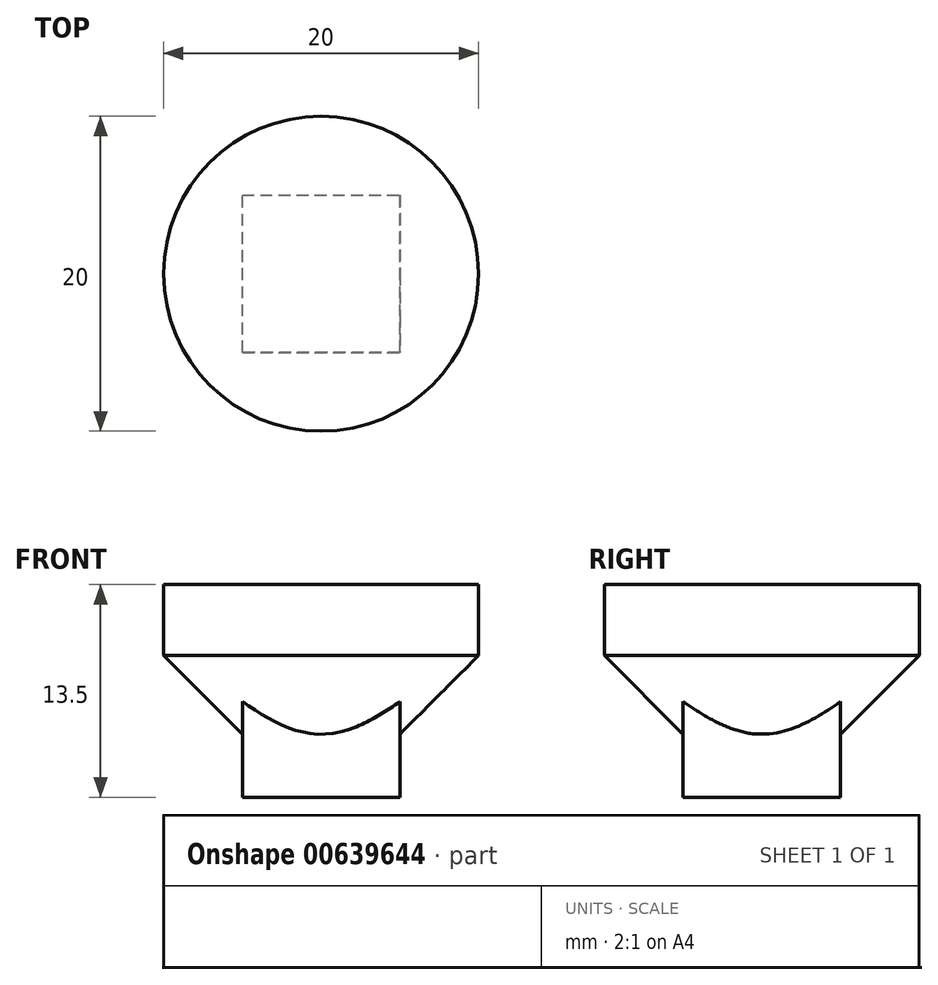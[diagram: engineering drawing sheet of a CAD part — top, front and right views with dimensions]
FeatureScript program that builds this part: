
annotation { "Feature Type Name" : "Feature", "Feature Type Description" : "" }
export const myFeature = defineFeature(function(context is Context, id is Id, definition is map)
    precondition{}
    {
        {
            var Q0;
            Q0=qCreatedBy(makeId("Top.planeOp"),FACE);
            var sketch = newSketch(context, id + "F0", { "sketchPlane" : qUnion([Q0])});
            skPoint(sketch, "E0.middle", {"position": v(0, 0) * mm});
            skLineSegment(sketch, "E1.bottom", {"start": v(5, 5) * mm, "end": v(-5, 5) * mm});
            skLineSegment(sketch, "E1.top", {"start": v(5, -5) * mm, "end": v(-5, -5) * mm});
            skLineSegment(sketch, "E1.left", {"start": v(5, 5) * mm, "end": v(5, -5) * mm});
            skLineSegment(sketch, "E1.right", {"start": v(-5, 5) * mm, "end": v(-5, -5) * mm});
            skLineSegment(sketch, "E2.bottom", {"start": v(-20.5, 20.5) * mm, "end": v(20.5, 20.5) * mm});
            skLineSegment(sketch, "E2.top", {"start": v(-20.5, -20.5) * mm, "end": v(20.5, -20.5) * mm});
            skLineSegment(sketch, "E2.left", {"start": v(-20.5, 20.5) * mm, "end": v(-20.5, -20.5) * mm});
            skLineSegment(sketch, "E2.right", {"start": v(20.5, 20.5) * mm, "end": v(20.5, -20.5) * mm});
            skSolve(sketch);
        }
        {
            var Q0;
            {var subQ1=sQuery(id+"F0.wireOp",EDGE,"E1.right");Q0=makeQuery(id+"F0.imprint","IMPRINT",FACE,{"disambiguationData":[TD([[makeQuery(id+"F0.imprint","IMPRINT",EDGE,{"derivedFrom":subQ1}),-1.0]])]});}
            var Q1;
            {var subQ1=sQuery(id+"F0.wireOp",EDGE,"E1.top");Q1=makeQuery(id+"F0.imprint","IMPRINT",FACE,{"disambiguationData":[TD([[makeQuery(id+"F0.imprint","IMPRINT",EDGE,{"derivedFrom":subQ1}),1.0]])]});}
            var Q2;
            {var subQ1=sQuery(id+"F0.wireOp",EDGE,"E1.left");Q2=makeQuery(id+"F0.imprint","IMPRINT",FACE,{"disambiguationData":[TD([[makeQuery(id+"F0.imprint","IMPRINT",EDGE,{"derivedFrom":subQ1}),1.0]])]});}
            var Q3;
            {var subQ5=sQuery(id+"F0.wireOp",EDGE,"E1.bottom");Q3=makeQuery(id+"F0.imprint","IMPRINT",FACE,{"disambiguationData":[TD([[makeQuery(id+"F0.imprint","IMPRINT",EDGE,{"derivedFrom":subQ5}),-1.0]])]});}
            var Q4;
            Q4=makeQuery(id+"F0.imprint","IMPRINT",FACE,{"disambiguationData":[TD([[makeQuery(id+"F0.imprint","IMPRINT",EDGE,{"derivedFrom":sQuery(id+"F0.wireOp",EDGE,"E1.bottom")}),1.0]])]});
            extrude(context, id + "F1", {"entities" : qUnion([Q0, Q1, Q2, Q3, Q4]), "depth" : 10 * mm, "offsetDistance" : 25 * mm});
        }
        {
            var Q0;
            Q0=makeQuery(id+"F0.imprint","IMPRINT",FACE,{"disambiguationData":[TD([[makeQuery(id+"F0.imprint","IMPRINT",EDGE,{"derivedFrom":sQuery(id+"F0.wireOp",EDGE,"E1.bottom")}),1.0]])]});
            extrude(context, id + "F2", {"entities" : qUnion([Q0]), "operationType" : NewBodyOperationType.ADD, "depth" : 25 * mm, "offsetDistance" : 25 * mm});
        }
        {
            var Q0;
            Q0=makeQuery(id+"F2.opExtrude","CAP_FACE",FACE,{"disambiguationData":[OSD([sQuery(id+"F0.wireOp",EDGE,"E1.bottom"),sQuery(id+"F0.wireOp",EDGE,"E1.top"),sQuery(id+"F0.wireOp",EDGE,"E1.left"),sQuery(id+"F0.wireOp",EDGE,"E1.right")])],"isStart":false});
            var sketch = newSketch(context, id + "F3", { "sketchPlane" : qUnion([Q0])});
            skLineSegment(sketch, "E3", {"start": v(-5, 5) * mm, "end": v(-5, -5) * mm});
            skPoint(sketch, "E4.middle", {"position": v(0, 0) * mm});
            skCircle(sketch, "E5", {"center": v(0, 0) * mm, "radius": 10 * mm});
            skSolve(sketch);
        }
        {
            var Q0;
            Q0=qSketchRegion(id+"F3",true);
            extrude(context, id + "F4", {"entities" : qUnion([Q0]), "operationType" : NewBodyOperationType.ADD, "oppositeDirection" : true, "depth" : 8 * mm, "offsetDistance" : 25 * mm});
        }
        {
            var Q0;
            Q0=makeQuery(id+"F1.opExtrude","CAP_FACE",FACE,{"disambiguationData":[OSD([sQuery(id+"F0.wireOp",EDGE,"E2.bottom"),sQuery(id+"F0.wireOp",EDGE,"E2.top"),sQuery(id+"F0.wireOp",EDGE,"E2.left"),sQuery(id+"F0.wireOp",EDGE,"E2.right")])],"isStart":true});
            var sketch = newSketch(context, id + "F5", { "sketchPlane" : qUnion([Q0])});
            skLineSegment(sketch, "E6.bottom", {"start": v(5, 5) * mm, "end": v(-5, 5) * mm});
            skLineSegment(sketch, "E6.top", {"start": v(5, -5) * mm, "end": v(-5, -5) * mm});
            skLineSegment(sketch, "E6.left", {"start": v(5, 5) * mm, "end": v(5, -5) * mm});
            skLineSegment(sketch, "E6.right", {"start": v(-5, 5) * mm, "end": v(-5, -5) * mm});
            skPoint(sketch, "E6.middle", {"position": v(0, 0) * mm});
            skPoint(sketch, "E7", {"position": v(5, 5) * mm});
            skPoint(sketch, "E8", {"position": v(-5, 5) * mm});
            skPoint(sketch, "E9", {"position": v(-5, -5) * mm});
            skPoint(sketch, "E10", {"position": v(5, -5) * mm});
            skLineSegment(sketch, "E11", {"start": v(0, 16.62) * mm, "end": v(0, 20.5) * mm});
            skLineSegment(sketch, "E12", {"start": v(-16.62, 0) * mm, "end": v(-20.5, 0) * mm});
            skLineSegment(sketch, "E13", {"start": v(0, -16.62) * mm, "end": v(0, -20.5) * mm});
            skLineSegment(sketch, "E14", {"start": v(16.62, 0) * mm, "end": v(20.5, 0) * mm});
            skArc(sketch, "E15", {"start": v(0, -20.5) * mm, "mid": v(13.15, -14.18) * mm, "end": v(16.62, 0) * mm});
            skArc(sketch, "E16", {"start": v(20.5, 0) * mm, "mid": v(14.2, 13.18) * mm, "end": v(0, 16.62) * mm});
            skArc(sketch, "E17", {"start": v(0, 20.5) * mm, "mid": v(-13.16, 14.18) * mm, "end": v(-16.62, 0) * mm});
            skArc(sketch, "E18", {"start": v(-20.5, 0) * mm, "mid": v(-14.2, -13.17) * mm, "end": v(0, -16.62) * mm});
            skSolve(sketch);
        }
        {
            var Q0;
            {var subQ0=sQuery(id+"F5.wireOp",EDGE,"E11");Q0=makeQuery(id+"F5.imprint","IMPRINT",FACE,{"disambiguationData":[TD([[makeQuery(id+"F5.imprint","IMPRINT",EDGE,{"derivedFrom":subQ0}),-1.0]])]});}
            var Q1;
            {var subQ0=sQuery(id+"F5.wireOp",EDGE,"E14");Q1=makeQuery(id+"F5.imprint","IMPRINT",FACE,{"disambiguationData":[TD([[makeQuery(id+"F5.imprint","IMPRINT",EDGE,{"derivedFrom":subQ0}),-1.0]])]});}
            var Q2;
            {var subQ0=sQuery(id+"F5.wireOp",EDGE,"E13");Q2=makeQuery(id+"F5.imprint","IMPRINT",FACE,{"disambiguationData":[TD([[makeQuery(id+"F5.imprint","IMPRINT",EDGE,{"derivedFrom":subQ0}),-1.0]])]});}
            var Q3;
            {var subQ0=sQuery(id+"F5.wireOp",EDGE,"E12");Q3=makeQuery(id+"F5.imprint","IMPRINT",FACE,{"disambiguationData":[TD([[makeQuery(id+"F5.imprint","IMPRINT",EDGE,{"derivedFrom":subQ0}),-1.0]])]});}
            extrude(context, id + "F6", {"entities" : qUnion([Q0, Q1, Q2, Q3]), "operationType" : NewBodyOperationType.REMOVE, "oppositeDirection" : true, "depth" : 25 * mm, "offsetDistance" : 25 * mm});
        }
        {
            var Q0;
            Q0=makeQuery(id+"F4.boolean.opBoolean","MERGE",FACE,{"derivedFrom":[makeQuery(id+"F2.opExtrude","CAP_FACE",FACE,{"disambiguationData":[OSD([sQuery(id+"F0.wireOp",EDGE,"E1.bottom"),sQuery(id+"F0.wireOp",EDGE,"E1.top"),sQuery(id+"F0.wireOp",EDGE,"E1.left"),sQuery(id+"F0.wireOp",EDGE,"E1.right")])],"isStart":false}),makeQuery(id+"F4.opExtrude","CAP_FACE",FACE,{"disambiguationData":[OSD([sQuery(id+"F3.wireOp",EDGE,"E5")])],"isStart":true})]});
            extrude(context, id + "F7", {"entities" : qUnion([Q0]), "operationType" : NewBodyOperationType.REMOVE, "oppositeDirection" : true, "depth" : 1.5 * mm, "offsetDistance" : 25 * mm});
        }
        {
            var Q0;
            Q0=makeQuery(id+"F1.opExtrude","CAP_FACE",FACE,{"disambiguationData":[OSD([sQuery(id+"F0.wireOp",EDGE,"E2.bottom"),sQuery(id+"F0.wireOp",EDGE,"E2.top"),sQuery(id+"F0.wireOp",EDGE,"E2.left"),sQuery(id+"F0.wireOp",EDGE,"E2.right")])],"isStart":true});
            extrude(context, id + "F8", {"entities" : qUnion([Q0]), "operationType" : NewBodyOperationType.REMOVE, "oppositeDirection" : true, "depth" : 10 * mm, "offsetDistance" : 25 * mm});
        }
        {
            var Q0;
            Q0=makeQuery(id+"F4.opExtrude","CAP_FACE",FACE,{"disambiguationData":[OSD([sQuery(id+"F3.wireOp",EDGE,"E5")])],"isStart":false});
            extrude(context, id + "F9", {"entities" : qUnion([Q0]), "operationType" : NewBodyOperationType.ADD, "depth" : 3 * mm, "offsetDistance" : 25 * mm});
        }
        {
            var Q0;
            Q0=makeQuery(id+"F9.opExtrude","CAP_EDGE",EDGE,{"disambiguationData":[OSD([sQuery(id+"F3.wireOp",EDGE,"E5")])],"isStart":false});
            chamfer(context, id + "F10", {"entities" : qUnion([Q0]), "width" : 5 * mm, "tangentPropagation" : true});
        }
    });
